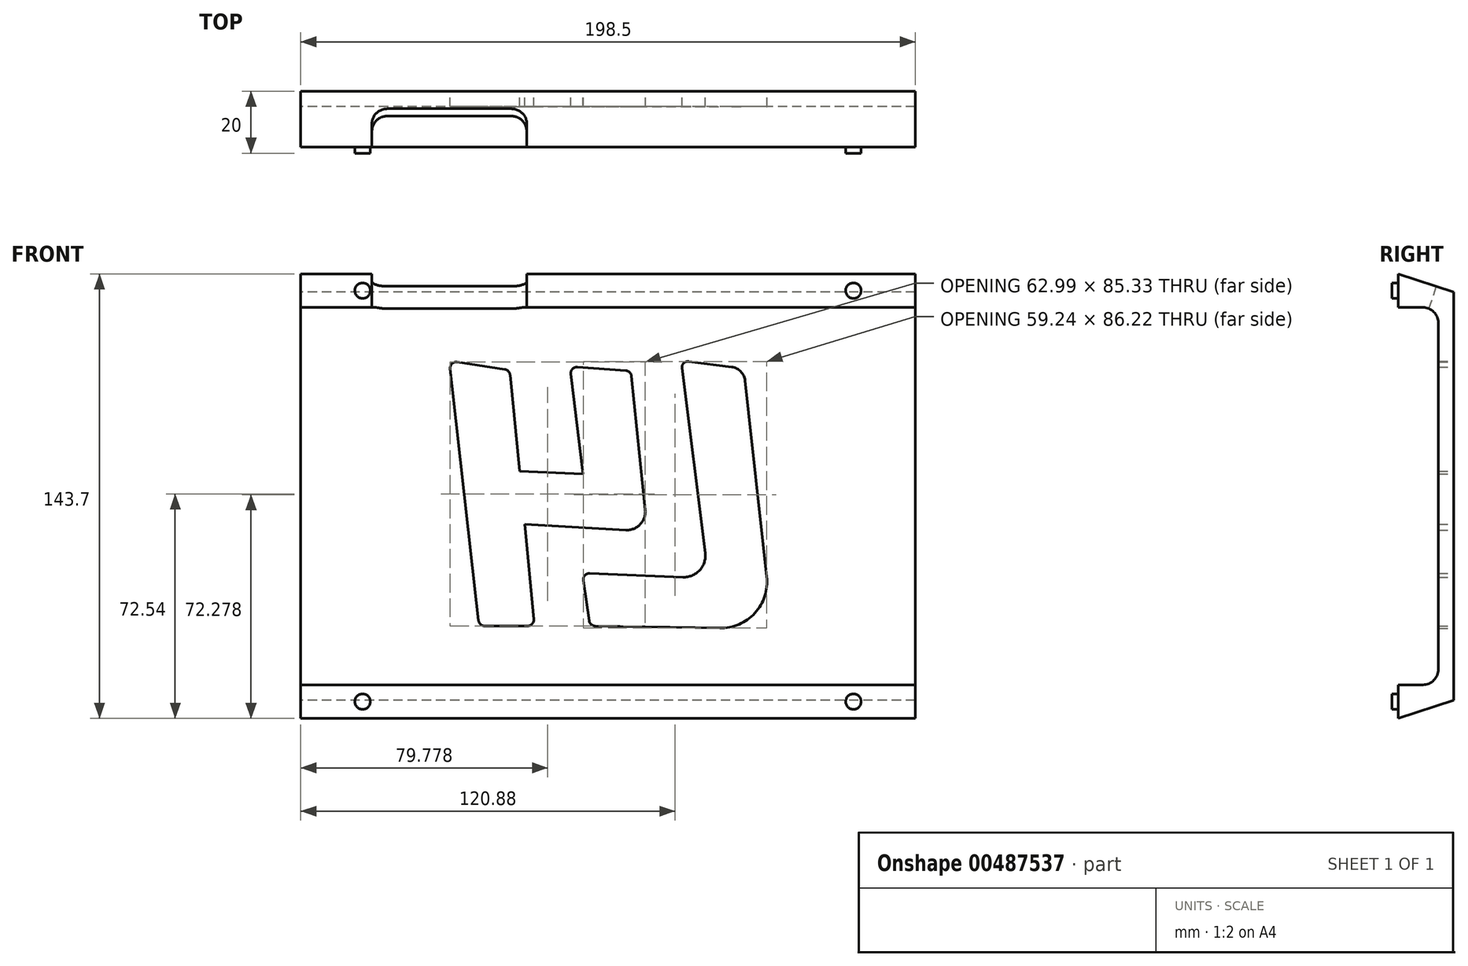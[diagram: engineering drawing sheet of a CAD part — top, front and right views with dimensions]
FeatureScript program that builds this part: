
annotation { "Feature Type Name" : "Feature", "Feature Type Description" : "" }
export const myFeature = defineFeature(function(context is Context, id is Id, definition is map)
    precondition{}
    {
        {
            var Q0;
            Q0=qCreatedBy(makeId("Right.planeOp"),FACE);
            var sketch = newSketch(context, id + "F0", { "sketchPlane" : qUnion([Q0])});
            skLineSegment(sketch, "E0", {"start": v(0, 66) * mm, "end": v(0, -66) * mm});
            skLineSegment(sketch, "E1", {"start": v(0, -66) * mm, "end": v(-18, -71.85) * mm});
            skLineSegment(sketch, "E2", {"start": v(-18, -71.85) * mm, "end": v(-18, 71.85) * mm});
            skLineSegment(sketch, "E3", {"start": v(-18, 71.85) * mm, "end": v(0, 66) * mm});
            skPoint(sketch, "E4", {"position": v(-18, 0) * mm});
            skLineSegment(sketch, "E5", {"start": v(47.78, 0) * mm, "end": v(-44.13, 0) * mm});
            skLineSegment(sketch, "E6", {"start": v(-5, 56) * mm, "end": v(-5, -56) * mm});
            skLineSegment(sketch, "E7", {"start": v(-10, -61) * mm, "end": v(-18, -61) * mm});
            skLineSegment(sketch, "E8", {"start": v(-10, 61) * mm, "end": v(-18, 61) * mm});
            skPoint(sketch, "E9", {"position": v(-5, 0) * mm});
            skPoint(sketch, "E10.visualSharp", {"position": v(-5, 61) * mm});
            skArc(sketch, "E10.filletArc", {"start": v(-5, 56) * mm, "mid": v(-6.46, 59.54) * mm, "end": v(-10, 61) * mm});
            skPoint(sketch, "E11.visualSharp", {"position": v(-5, -61) * mm});
            skArc(sketch, "E11.filletArc", {"start": v(-10, -61) * mm, "mid": v(-6.46, -59.54) * mm, "end": v(-5, -56) * mm});
            skSolve(sketch);
        }
        {
            var Q0;
            {var subQ5=sQuery(id+"F0.wireOp",EDGE,"E3");Q0=makeQuery(id+"F0.imprint","IMPRINT",FACE,{"disambiguationData":[TD([[makeQuery(id+"F0.imprint","IMPRINT",EDGE,{"derivedFrom":subQ5}),-1.0]])]});}
            var Q1;
            {var subQ6=sQuery(id+"F0.wireOp",EDGE,"E1");Q1=makeQuery(id+"F0.imprint","IMPRINT",FACE,{"disambiguationData":[TD([[makeQuery(id+"F0.imprint","IMPRINT",EDGE,{"derivedFrom":subQ6}),-1.0]])]});}
            var Q2;
            Q2 = qSketchRegion(id + "F7", true);
            extrude(context, id + "F1", {"entities" : qUnion([Q0, Q1, Q2]), "endBound" : BoundingType.SYMMETRIC, "depth" : 198.5 * mm, "offsetDistance" : 25 * mm});
        }
        {
            var Q0;
            {var subQ0=sQuery(id+"F0.wireOp",EDGE,"E2");Q0=makeQuery(id+"F1.opExtrude","SWEPT_FACE",FACE,{"disambiguationData":[OSD([subQ0]),TDD([makeQuery(id+"F0.imprint","IMPRINT",EDGE,{"disambiguationData":[TD([[makeQuery(id+"F0.imprint","INTERSECT",VERTEX,{"derivedFrom":[subQ0,sQuery(id+"F0.wireOp",EDGE,"E3")]}),1.0]])],"derivedFrom":subQ0})])]});}
            var sketch = newSketch(context, id + "F2", { "sketchPlane" : qUnion([Q0])});
            skLineSegment(sketch, "E12", {"start": v(-79.25, 71.85) * mm, "end": v(-79.25, 61) * mm});
            skPoint(sketch, "E13", {"position": v(-79.25, 66.42) * mm});
            skCircle(sketch, "E14", {"center": v(-79.25, 66.42) * mm, "radius": 2.5 * mm});
            skLineSegment(sketch, "E15", {"start": v(79.25, 71.85) * mm, "end": v(79.25, 61) * mm});
            skPoint(sketch, "E16", {"position": v(79.25, 66.42) * mm});
            skCircle(sketch, "E17", {"center": v(79.25, 66.42) * mm, "radius": 2.5 * mm});
            skSolve(sketch);
        }
        {
            var Q0;
            {var subQ0=sQuery(id+"F0.wireOp",EDGE,"E2");Q0=makeQuery(id+"F1.opExtrude","SWEPT_FACE",FACE,{"disambiguationData":[OSD([subQ0]),TDD([makeQuery(id+"F0.imprint","IMPRINT",EDGE,{"disambiguationData":[TD([[makeQuery(id+"F0.imprint","INTERSECT",VERTEX,{"derivedFrom":[sQuery(id+"F0.wireOp",EDGE,"E1"),subQ0]}),-1.0]])],"derivedFrom":subQ0})])]});}
            var sketch = newSketch(context, id + "F3", { "sketchPlane" : qUnion([Q0])});
            skLineSegment(sketch, "E18", {"start": v(-79.25, -61) * mm, "end": v(-79.25, -71.85) * mm});
            skPoint(sketch, "E19", {"position": v(-79.25, -66.42) * mm});
            skLineSegment(sketch, "E20", {"start": v(79.25, -61) * mm, "end": v(79.25, -71.85) * mm});
            skPoint(sketch, "E21", {"position": v(79.25, -66.42) * mm});
            skCircle(sketch, "E22", {"center": v(-79.25, -66.42) * mm, "radius": 2.5 * mm});
            skCircle(sketch, "E23", {"center": v(79.25, -66.42) * mm, "radius": 2.5 * mm});
            skSolve(sketch);
        }
        {
            var Q0;
            Q0=qSketchRegion(id+"F3",true);
            var Q1;
            {var subQ0=sQuery(id+"F2.wireOp",EDGE,"E14");var subQ1=sQuery(id+"F2.wireOp",EDGE,"E12");var subQ2=makeQuery(id+"F2.imprint","INTERSECT",VERTEX,{"disambiguationData":[OD(0.0)],"derivedFrom":[subQ1,subQ0]});Q1=makeQuery(id+"F2.imprint","IMPRINT",FACE,{"disambiguationData":[TD([[makeQuery(id+"F2.imprint","IMPRINT",EDGE,{"disambiguationData":[TD([[subQ2,-1.0]])],"derivedFrom":subQ1}),-1.0]])]});}
            var Q2;
            {var subQ0=sQuery(id+"F2.wireOp",EDGE,"E14");var subQ1=sQuery(id+"F2.wireOp",EDGE,"E12");var subQ2=makeQuery(id+"F2.imprint","INTERSECT",VERTEX,{"disambiguationData":[OD(0.0)],"derivedFrom":[subQ1,subQ0]});Q2=makeQuery(id+"F2.imprint","IMPRINT",FACE,{"disambiguationData":[TD([[makeQuery(id+"F2.imprint","IMPRINT",EDGE,{"disambiguationData":[TD([[subQ2,-1.0]])],"derivedFrom":subQ1}),1.0]])]});}
            var Q3;
            {var subQ0=sQuery(id+"F2.wireOp",EDGE,"E17");var subQ1=sQuery(id+"F2.wireOp",EDGE,"E15");var subQ2=makeQuery(id+"F2.imprint","INTERSECT",VERTEX,{"disambiguationData":[OD(0.0)],"derivedFrom":[subQ1,subQ0]});Q3=makeQuery(id+"F2.imprint","IMPRINT",FACE,{"disambiguationData":[TD([[makeQuery(id+"F2.imprint","IMPRINT",EDGE,{"disambiguationData":[TD([[subQ2,-1.0]])],"derivedFrom":subQ1}),-1.0]])]});}
            var Q4;
            {var subQ0=sQuery(id+"F2.wireOp",EDGE,"E17");var subQ1=sQuery(id+"F2.wireOp",EDGE,"E15");var subQ2=makeQuery(id+"F2.imprint","INTERSECT",VERTEX,{"disambiguationData":[OD(0.0)],"derivedFrom":[subQ1,subQ0]});Q4=makeQuery(id+"F2.imprint","IMPRINT",FACE,{"disambiguationData":[TD([[makeQuery(id+"F2.imprint","IMPRINT",EDGE,{"disambiguationData":[TD([[subQ2,-1.0]])],"derivedFrom":subQ1}),1.0]])]});}
            extrude(context, id + "F4", {"entities" : qUnion([Q0, Q1, Q2, Q3, Q4]), "operationType" : NewBodyOperationType.ADD, "depth" : 2 * mm});
        }
        {
            var Q0;
            Q0=makeQuery(id+"F1.opExtrude","SWEPT_FACE",FACE,{"disambiguationData":[OSD([sQuery(id+"F0.wireOp",EDGE,"E3")])]});
            var sketch = newSketch(context, id + "F5", { "sketchPlane" : qUnion([Q0])});
            skLineSegment(sketch, "E24.bottom", {"start": v(-71.25, -26.32) * mm, "end": v(-31.25, -26.32) * mm});
            skLineSegment(sketch, "E24.top", {"start": v(-76.25, -39.32) * mm, "end": v(-26.25, -39.32) * mm});
            skLineSegment(sketch, "E24.left", {"start": v(-76.25, -31.32) * mm, "end": v(-76.25, -39.32) * mm});
            skLineSegment(sketch, "E24.right", {"start": v(-26.25, -31.32) * mm, "end": v(-26.25, -39.32) * mm});
            skPoint(sketch, "E25.visualSharp", {"position": v(-76.25, -26.32) * mm});
            skArc(sketch, "E25.filletArc", {"start": v(-71.25, -26.32) * mm, "mid": v(-74.79, -27.79) * mm, "end": v(-76.25, -31.32) * mm});
            skPoint(sketch, "E26.visualSharp", {"position": v(-26.25, -26.32) * mm});
            skArc(sketch, "E26.filletArc", {"start": v(-26.25, -31.32) * mm, "mid": v(-27.71, -27.79) * mm, "end": v(-31.25, -26.32) * mm});
            skSolve(sketch);
        }
        {
            var Q0;
            Q0=makeQuery(id+"F5.imprint","IMPRINT",FACE,{"disambiguationData":[TD([[makeQuery(id+"F5.imprint","IMPRINT",EDGE,{"derivedFrom":sQuery(id+"F5.wireOp",EDGE,"E24.bottom")}),-1.0]])]});
            extrude(context, id + "F6", {"entities" : qUnion([Q0]), "operationType" : NewBodyOperationType.REMOVE, "oppositeDirection" : true, "depth" : 12 * mm, "offsetDistance" : 25 * mm});
        }
        {
            var Q0;
            Q0=makeQuery(id+"F1.opExtrude","SWEPT_FACE",FACE,{"disambiguationData":[OSD([sQuery(id+"F0.wireOp",EDGE,"E0")])]});
            var sketch = newSketch(context, id + "F7", { "sketchPlane" : qUnion([Q0])});
            skPoint(sketch, "E27", {"position": v(0, 75) * mm});
            skPoint(sketch, "E28", {"position": v(-82.72, 0) * mm});
            skLineSegment(sketch, "E29", {"start": v(-39.95, 41.73) * mm, "end": v(-26.12, 43.53) * mm});
            skLineSegment(sketch, "E30", {"start": v(-23.88, 41.3) * mm, "end": v(-31.39, -18.33) * mm});
            skLineSegment(sketch, "E31", {"start": v(-24.16, -26.2) * mm, "end": v(5.92, -24.98) * mm});
            skLineSegment(sketch, "E32", {"start": v(7.98, -27.26) * mm, "end": v(6.07, -40.3) * mm});
            skLineSegment(sketch, "E33", {"start": v(4.12, -42) * mm, "end": v(-36.08, -42.68) * mm});
            skLineSegment(sketch, "E34", {"start": v(-51.24, -26.05) * mm, "end": v(-44.27, 37.32) * mm});
            skPoint(sketch, "E35.visualSharp", {"position": v(-43.84, 41.22) * mm});
            skArc(sketch, "E35.filletArc", {"start": v(-39.95, 41.73) * mm, "mid": v(-42.87, 40.27) * mm, "end": v(-44.27, 37.32) * mm});
            skPoint(sketch, "E36.visualSharp", {"position": v(-23.56, 43.87) * mm});
            skArc(sketch, "E36.filletArc", {"start": v(-23.88, 41.3) * mm, "mid": v(-24.45, 42.97) * mm, "end": v(-26.12, 43.53) * mm});
            skPoint(sketch, "E37.visualSharp", {"position": v(-53.1, -42.97) * mm});
            skArc(sketch, "E37.filletArc", {"start": v(-51.24, -26.05) * mm, "mid": v(-47.42, -37.8) * mm, "end": v(-36.08, -42.68) * mm});
            skPoint(sketch, "E38.visualSharp", {"position": v(5.82, -41.98) * mm});
            skArc(sketch, "E38.filletArc", {"start": v(4.12, -42) * mm, "mid": v(5.41, -41.5) * mm, "end": v(6.07, -40.3) * mm});
            skPoint(sketch, "E39.visualSharp", {"position": v(8.32, -24.88) * mm});
            skArc(sketch, "E39.filletArc", {"start": v(7.98, -27.26) * mm, "mid": v(7.48, -25.64) * mm, "end": v(5.92, -24.98) * mm});
            skPoint(sketch, "E40.visualSharp", {"position": v(-32.42, -26.53) * mm});
            skArc(sketch, "E40.filletArc", {"start": v(-31.39, -18.33) * mm, "mid": v(-29.6, -23.94) * mm, "end": v(-24.16, -26.2) * mm});
            skLineSegment(sketch, "E41", {"start": v(-7.56, 38.8) * mm, "end": v(-12.02, -4.37) * mm});
            skLineSegment(sketch, "E42", {"start": v(-5.71, -10.98) * mm, "end": v(26.82, -9.12) * mm});
            skLineSegment(sketch, "E43", {"start": v(26.82, -9.12) * mm, "end": v(23.97, -39.79) * mm});
            skLineSegment(sketch, "E44", {"start": v(25.96, -41.97) * mm, "end": v(39.83, -41.97) * mm});
            skLineSegment(sketch, "E45", {"start": v(41.81, -40.2) * mm, "end": v(50.97, 41.14) * mm});
            skLineSegment(sketch, "E46", {"start": v(48.67, 43.34) * mm, "end": v(33.3, 40.96) * mm});
            skLineSegment(sketch, "E47", {"start": v(31.62, 39.18) * mm, "end": v(28.55, 8.1) * mm});
            skLineSegment(sketch, "E48", {"start": v(28.55, 8.1) * mm, "end": v(8.1, 7.14) * mm});
            skLineSegment(sketch, "E49", {"start": v(8.1, 7.14) * mm, "end": v(12, 39.5) * mm});
            skLineSegment(sketch, "E50", {"start": v(9.87, 41.73) * mm, "end": v(-5.72, 40.59) * mm});
            skPoint(sketch, "E51.visualSharp", {"position": v(-12.75, -11.38) * mm});
            skArc(sketch, "E51.filletArc", {"start": v(-12.02, -4.37) * mm, "mid": v(-10.4, -9.13) * mm, "end": v(-5.71, -10.98) * mm});
            skPoint(sketch, "E52.visualSharp", {"position": v(23.77, -41.97) * mm});
            skArc(sketch, "E52.filletArc", {"start": v(23.97, -39.79) * mm, "mid": v(24.49, -41.32) * mm, "end": v(25.96, -41.97) * mm});
            skPoint(sketch, "E53.visualSharp", {"position": v(41.61, -41.97) * mm});
            skArc(sketch, "E53.filletArc", {"start": v(39.83, -41.97) * mm, "mid": v(41.16, -41.47) * mm, "end": v(41.81, -40.2) * mm});
            skPoint(sketch, "E54.visualSharp", {"position": v(51.26, 43.74) * mm});
            skArc(sketch, "E54.filletArc", {"start": v(50.97, 41.14) * mm, "mid": v(50.36, 42.8) * mm, "end": v(48.67, 43.34) * mm});
            skPoint(sketch, "E55.visualSharp", {"position": v(31.77, 40.72) * mm});
            skArc(sketch, "E55.filletArc", {"start": v(33.3, 40.96) * mm, "mid": v(32.16, 40.36) * mm, "end": v(31.62, 39.18) * mm});
            skPoint(sketch, "E56.visualSharp", {"position": v(12.3, 41.9) * mm});
            skArc(sketch, "E56.filletArc", {"start": v(12, 39.5) * mm, "mid": v(11.46, 41.11) * mm, "end": v(9.87, 41.73) * mm});
            skPoint(sketch, "E57.visualSharp", {"position": v(-7.4, 40.46) * mm});
            skArc(sketch, "E57.filletArc", {"start": v(-5.72, 40.59) * mm, "mid": v(-6.97, 40.03) * mm, "end": v(-7.56, 38.8) * mm});
            skSolve(sketch);
        }
        {
            var Q0;
            Q0 = qSketchRegion(id + "F7", true);
            extrude(context, id + "F8", {"entities" : qUnion([Q0]), "operationType" : NewBodyOperationType.REMOVE, "oppositeDirection" : true, "depth" : 10 * mm, "offsetDistance" : 25 * mm});
        }
    });
